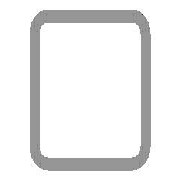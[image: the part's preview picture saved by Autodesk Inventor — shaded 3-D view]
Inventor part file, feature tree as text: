
AUTODESK INVENTOR PART (.ipt)
format: ipt  version: 2022 (Build 260153000, 153)  size: 146,944 bytes
history: native  units: mm (DEFAULTED — no unit token found)
features: other x4, plane x3, sketch x3, split x2
ambient origin geometry x8: Origin, YZ Plane, XZ Plane, XY Plane, X Axis, Y Axis, Z Axis, Center Point
bodies: Solid1 (feature_tree), Body (feature_tree)
feature tree (12):
  parser-record x1  (decoder bookkeeping rows leaked as tree rows — omitted from the tree; the rows remain in map.json)
  other  "Driven Length"
  other  "Start Plane"
  other  "End Plane"
  plane  "Work Plane4"
  split  "Split1"
  plane  "Work Plane5"
  split  "Split2"
  sketch  "Sketch"  dims[d7=8.0mm d9=40.0mm d11=40.0mm d12=4.0mm d13=20.0mm d14=118.284271mm d15=20.0mm d16=20.0mm d17=90.0deg d18=98.284271mm]
  sketch  "Sketch3"  dims[d3=98.284271mm]
  plane  "Work Plane3"
  sketch  "Sketch4"  dims[d4=0.0mm]
